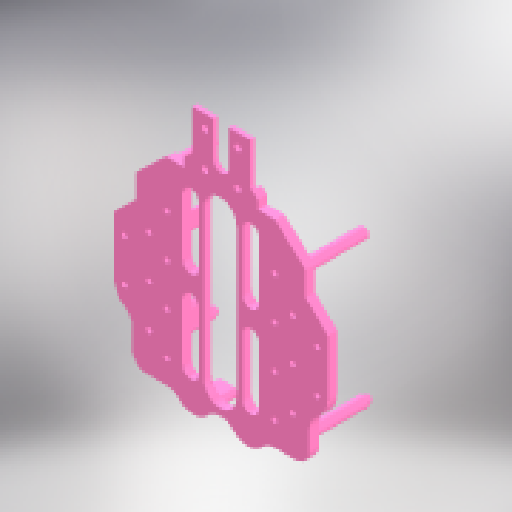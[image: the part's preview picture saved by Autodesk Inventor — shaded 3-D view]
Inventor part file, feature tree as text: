
AUTODESK INVENTOR PART (.ipt)
format: ipt  version: 2025.2 (Build 292293000, 293)  size: 1,608,704 bytes
history: native  units: mm
features: sketch x56, extrude x53, reference x41, other x16, fillet x15, projected_geometry x10, plane x5
ambient origin geometry x8: Origin, YZ Plane, XZ Plane, XY Plane, X Axis, Y Axis, Z Axis, Center Point
bodies: Solid1 (feature_tree)
feature tree (196):
  plane  "Work Plane1"
  extrude  "Extrusion1"  Depth=2.0mm
  extrude  "Extrusion2"  Depth=25.0mm
  extrude  "Extrusion3"  Depth=5.0mm TaperAngle=0.0deg
  extrude  "Extrusion4"  Depth=3.0mm TaperAngle=0.0deg
  extrude  "Extrusion5"  Depth=0.25mm
  extrude  "Extrusion6"  Depth=5.0mm TaperAngle=0.0deg
  extrude  "Extrusion7"  Depth=2.0mm TaperAngle=0.0deg
  fillet  "Fillet1"  Radius=2.0mm
  extrude  "Extrusion8"  TaperAngle=0.0deg  [1 undecoded]
  fillet  "Fillet2"  Radius=13.75mm
  fillet  "Fillet3"  [1 undecoded]
  extrude  "Extrusion9"  Depth=10.0mm
  extrude  "Extrusion10"  Depth=10.0mm TaperAngle=0.0deg
  extrude  "Extrusion11"  Depth=10.0mm TaperAngle=0.0deg
  extrude  "Extrusion12"  TaperAngle=0.0deg  [1 undecoded]
  extrude  "Extrusion13"  Depth=10.0mm TaperAngle=0.0deg
  extrude  "Extrusion14"  TaperAngle=0.0deg  [1 undecoded]
  extrude  "Extrusion15"  TaperAngle=0.0deg  [1 undecoded]
  extrude  "Extrusion16"  Depth=51.25mm TaperAngle=0.0deg
  extrude  "Extrusion17"  Depth=4.0mm
  extrude  "Extrusion18"  TaperAngle=0.0deg  [1 undecoded]
  extrude  "Extrusion19"  Depth=6.25mm
  extrude  "Extrusion20"  Depth=10.0mm
  extrude  "Extrusion21"  Depth=10.0mm TaperAngle=0.0deg
  extrude  "Extrusion22"  Depth=10.0mm TaperAngle=0.0deg
  extrude  "Extrusion23"  Depth=6.25mm
  fillet  "Fillet4"  [1 undecoded]
  extrude  "Extrusion24"  Depth=10.0mm TaperAngle=0.0deg
  extrude  "Extrusion25"  Depth=2.0mm TaperAngle=0.0deg
  extrude  "Extrusion26"  TaperAngle=0.0deg  [1 undecoded]
  extrude  "Extrusion27"  Depth=10.0mm TaperAngle=0.0deg
  fillet  "Fillet5"  [1 undecoded]
  fillet  "Fillet6"  Radius=23.25mm
  extrude  "Extrusion28"  Depth=1.0mm
  extrude  "Extrusion29"  Depth=1.0mm TaperAngle=0.0deg
  fillet  "Fillet7"  Radius=37.73mm
  sketch  "Sketch31"  dims[d122=2.5mm d123=41.976mm]
  plane  "Work Plane2"
  extrude  "Extrusion30"  Depth=37.73mm
  sketch  "Sketch32"  dims[d124=10.5mm d125=0.0mm d126=2.0mm]
  extrude  "Extrusion31"  Depth=2.0mm
  extrude  "Extrusion32"  Depth=41.976mm
  extrude  "Extrusion33"  Depth=2.0mm
  extrude  "Extrusion35"  Depth=10.0mm
  extrude  "Extrusion36"  Depth=10.0mm
  extrude  "Extrusion37"  Depth=10.0mm
  extrude  "Extrusion38"  TaperAngle=0.0deg  [1 undecoded]
  extrude  "Extrusion39"  Depth=1.0mm TaperAngle=0.0deg
  extrude  "Extrusion40"  Depth=3.1mm
  fillet  "Fillet8"  Radius=3.1mm
  extrude  "Extrusion41"  Depth=10.0mm TaperAngle=0.0deg
  extrude  "Extrusion42"  Depth=2.0mm TaperAngle=0.0deg
  fillet  "Fillet9"  Radius=2.0mm
  extrude  "Extrusion43"  Depth=4.7mm
  extrude  "Extrusion44"  Depth=10.0mm TaperAngle=0.0deg
  fillet  "Fillet10"  Radius=1.0mm
  extrude  "Extrusion45"  Depth=1.0mm
  fillet  "Fillet11"  [1 undecoded]
  plane  "Work Plane3"
  plane  "Work Plane4"
  sketch  "Sketch51"  dims[d178=0.5mm d179=0.872665mm]
  plane  "Work Plane5"
  extrude  "Extrusion49"  Depth=8.756743mm
  extrude  "Extrusion50"  Depth=3.769mm
  fillet  "Fillet15"  [1 undecoded]
  extrude  "Extrusion53"  Depth=4.0mm
  extrude  "Extrusion54"  Depth=0.872665mm
  extrude  "Extrusion55"  Depth=0.872665mm
  fillet  "Fillet16"  [1 undecoded]
  extrude  "Extrusion56"  [1 undecoded]
  fillet  "Fillet17"  [1 undecoded]
  extrude  "Extrusion57"  [1 undecoded]
  extrude  "Extrusion58"  [1 undecoded]
  extrude  "Extrusion59"  [1 undecoded]
  fillet  "Fillet18"  [1 undecoded]
  sketch  "Sketch1"  dims[d2=2.0mm d3=75.55mm]
  reference  "Reference1"
  reference  "Reference2"
  reference  "Reference3"
  reference  "Reference4"
  reference  "Reference5"
  reference  "Reference6"
  reference  "Reference7"
  reference  "Reference8"
  reference  "Reference9"
  reference  "Reference10"
  sketch  "Sketch2"  dims[d7=25.0mm d8=5.0mm d9=0.0mm]
  reference  "Reference11"
  reference  "Reference12"
  reference  "Reference13"
  reference  "Reference14"
  sketch  "Sketch3"  dims[d13=0.25mm d14=0.25mm]
  reference  "Reference15"
  reference  "Reference16"
  reference  "Reference17"
  sketch  "Sketch4"  dims[d15=0.25mm d16=5.0mm d17=0.0mm]
  reference  "Reference18"
  reference  "Reference19"
  reference  "Reference20"
  reference  "Reference21"
  reference  "Reference22"
  sketch  "Sketch5"  dims[d18=5.0mm d19=5.0mm d20=0.0mm d21=2.0mm d22=0.0mm]
  sketch  "Sketch6"  dims[d23=0.0mm d24=0.0mm d25=0.0mm d26=0.0mm d27=13.75mm d28=0.0mm d29=0.0mm]
  sketch  "Sketch7"  dims[d30=35.25mm d31=10.0mm]
  sketch  "Sketch8"  dims[d32=8.0mm d33=10.0mm d34=0.0mm]
  reference  "Reference23"
  reference  "Reference24"
  sketch  "Sketch10"  dims[d35=0.0mm d36=0.0mm d37=10.0mm d38=0.0mm]
  reference  "Reference30"
  sketch  "Sketch11"  dims[d39=0.0mm d40=0.0mm d41=0.0mm d42=0.0mm]
  sketch  "Sketch12"  dims[d43=0.0mm d44=0.0mm d45=10.0mm d46=0.0mm]
  sketch  "Sketch13"  dims[d47=3.0mm d48=0.0mm d49=0.0mm d50=0.0mm]
  sketch  "Sketch14"  dims[d51=17.0mm d52=0.0mm d53=0.0mm d54=0.0mm]
  sketch  "Sketch15"  dims[d55=51.25mm d56=0.0mm d57=51.25mm d58=0.0mm]
  sketch  "Sketch16"  dims[d59=4.0mm d60=20.0mm]
  sketch  "Sketch17"  dims[d64=108.0mm d65=0.0mm d66=0.0mm]
  sketch  "Sketch18"  dims[d67=0.0mm d68=0.0mm d69=6.25mm]
  reference  "Reference31"
  reference  "Reference32"
  sketch  "Sketch19"  dims[d70=10.0mm d71=0.0mm d72=30.0mm]
  sketch  "Sketch20"  dims[d73=7.5mm d74=10.0mm d75=0.0mm]
  reference  "Reference33"
  reference  "Reference34"
  sketch  "Sketch21"  dims[d76=10.0mm d77=0.0mm d78=10.0mm d79=0.0mm]
  projected_geometry  "Projected Loop1"
  sketch  "Sketch22"  dims[d80=6.25mm d81=6.25mm d82=0.0mm d83=0.0mm]
  sketch  "Sketch23"  dims[d84=7.0mm d87=10.0mm d88=0.0mm]
  sketch  "Sketch24"  dims[d89=6.25mm d90=2.0mm d91=0.0mm]
  sketch  "Sketch25"  dims[d92=35.0mm d93=0.0mm d94=0.0mm]
  sketch  "Sketch26"  dims[d95=54.25mm d96=0.0mm d97=10.0mm d98=0.0mm d102=0.0mm d103=0.0mm d104=23.25mm d105=0.0mm]
  sketch  "Sketch27"  dims[d106=1.0mm d107=1.0mm]
  sketch  "Sketch28"  dims[d108=1.0mm d109=24.0mm d110=0.0mm d112=37.73mm]
  sketch  "Sketch29"  dims[d113=24.0mm d114=0.0mm d115=37.73mm]
  sketch  "Sketch30"  dims[d116=0.0mm d117=0.0mm d119=2.0mm]
  sketch  "Sketch33"  dims[d127=10.0mm d128=0.0mm d129=24.0mm]
  sketch  "Sketch34"  dims[d130=10.0mm d131=0.0mm d132=6.5mm]
  sketch  "Sketch35"  dims[d133=10.0mm d134=0.0mm d135=20.0mm d137=18.0mm d138=20.0mm d140=18.0mm]
  sketch  "Sketch37"  dims[d143=20.0mm d145=18.0mm d146=10.0mm d148=10.0mm d150=0.0mm d151=0.0mm]
  reference  "Reference35"
  reference  "Reference36"
  sketch  "Sketch38"  dims[d152=1.0mm d153=0.5mm d154=0.0mm]
  projected_geometry  "Projected Loop2"
  projected_geometry  "Projected Loop3"
  sketch  "Sketch39"  dims[d155=11.0mm d168=3.1mm d169=3.1mm]
  sketch  "Sketch40"  dims[d170=3.1mm d171=10.0mm d172=0.0mm]
  sketch  "Sketch41"  dims[d173=3.1mm d174=4.99mm d175=0.0mm d185=2.0mm]
  sketch  "Sketch42"  dims[d186=0.0mm d187=0.0mm d188=4.7mm]
  projected_geometry  "Projected Loop4"
  sketch  "Sketch43"  dims[d189=10.0mm d190=0.0mm d191=10.0mm d192=0.0mm d193=1.0mm]
  projected_geometry  "Projected Loop5"
  sketch  "Sketch44"  dims[d194=10.0mm d195=0.0mm d196=1.0mm d197=0.0mm d198=0.0mm]
  projected_geometry  "Projected Loop6"
  sketch  "Sketch45"  dims[d199=8.756743mm d200=9.607523mm]
  reference  "Reference37"
  reference  "Reference38"
  sketch  "Sketch Rectangular Pattern1"  dims[d4=72.5mm d6=25.0mm]
  sketch  "Sketch Rectangular Pattern2"  dims[d10=0.4mm d11=3.0mm d12=0.0mm]
  sketch  "Sketch46"  dims[d201=3.769438mm d202=3.769mm d203=0.0mm d204=0.0mm]
  sketch  "Sketch47"  dims[d205=10.0mm d206=0.0mm d207=4.0mm]
  reference  "Reference41"
  projected_geometry  "Projected Loop7"
  projected_geometry  "Projected Loop8"
  sketch  "Sketch52"  dims[d180=0.5mm d181=0.872665mm]
  projected_geometry  "Projected Loop9"
  projected_geometry  "Projected Loop10"
  sketch  "Sketch56"
  reference  "Reference42"
  reference  "Reference43"
  reference  "Reference44"
  sketch  "Sketch57"
  sketch  "Sketch58"
  sketch  "Sketch59"
  sketch  "Sketch60"
  reference  "Reference45"
  reference  "Reference46"
  sketch  "Sketch61"
  reference  "Reference47"
  sketch  "Sketch62"
  reference  "Reference48"
  other  "<userpath>\OneDrive\Dokumen\Prak.Robotika\board fix\Assembly3.iam"
  other  "Assembly3.iam"
  other  "main_board1:1"
  other  "board_ctrl:1"
  other  "motor mount-Body:1"
  other  "3D_SensorLF:1"
  other  "Board~uqsa_1"
  other  "motor mount-Body:3"
  other  "SENSOR_3D:1"
  other  "sensor:1"
  other  "<userpath>\OneDrive\Dokumen\Prak.Robotika\board fix\lf.iam"
  other  "lf.iam"
  other  "motor:2"
  other  "motor:1"
  other  "SENSOR_3D1:1"
  other  "Assembly3"
note: 19 required parameter values undecoded (feature->parameter linkage not recoverable at this tier; creation-order binding heuristic only, values carry confidence <= 0.55)
